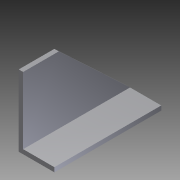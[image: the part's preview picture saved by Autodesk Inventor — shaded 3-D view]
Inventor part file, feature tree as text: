
AUTODESK INVENTOR PART (.ipt)
format: ipt  version: 2012 (Build 160160000, 160)  size: 84,480 bytes
history: native  units: in
note: dims shown in document units (in); Inventor stores cm internally (conversion verified against a paired STEP export)
features: extrude x2, sketch x2
ambient origin geometry x8: Origin, YZ Plane, XZ Plane, XY Plane, X Axis, Y Axis, Z Axis, Center Point
bodies: Solid1 (feature_tree)
feature tree (4):
  extrude  "Extrusion1"  Depth=1.0in
  extrude  "Extrusion2"  Depth=3.0in TaperAngle=0.0deg
  sketch  "Sketch1"  dims[d0=2.0in d1=1.0in]
  sketch  "Sketch2"  dims[d2=0.1242in d3=3.0in d4=0.0in d5=1.0in d6=0.125in d7=1.0in d8=0.0in]
